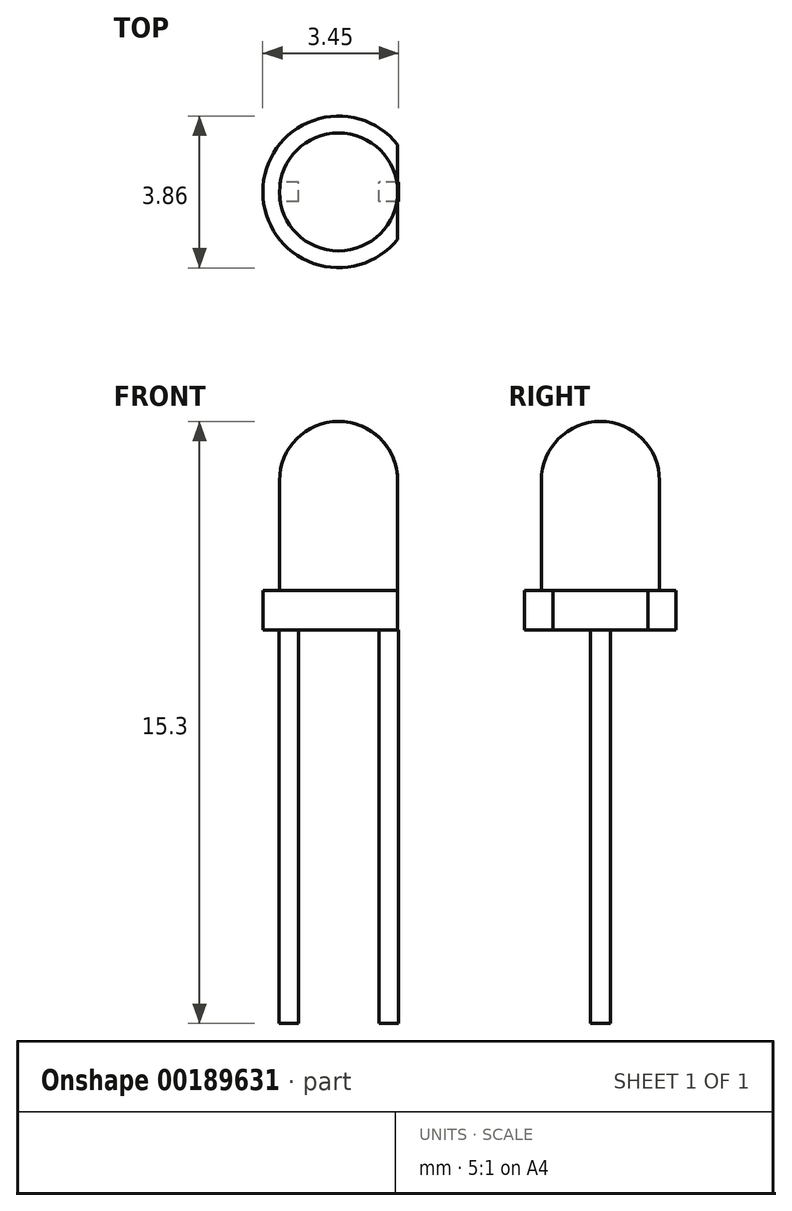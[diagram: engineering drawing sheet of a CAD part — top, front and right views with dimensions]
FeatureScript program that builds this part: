
annotation { "Feature Type Name" : "Feature", "Feature Type Description" : "" }
export const myFeature = defineFeature(function(context is Context, id is Id, definition is map)
    precondition{}
    {
        {
            var Q0;
            Q0=qCreatedBy(makeId("Front.planeOp"),FACE);
            var sketch = newSketch(context, id + "F0", { "sketchPlane" : qUnion([Q0])});
            skLineSegment(sketch, "E0", {"start": v(0, 0) * mm, "end": v(0, 5.3) * mm});
            skLineSegment(sketch, "E1", {"start": v(0, 0) * mm, "end": v(1.93, 0) * mm});
            skLineSegment(sketch, "E2", {"start": v(1.93, 0) * mm, "end": v(1.93, 1) * mm});
            skLineSegment(sketch, "E3", {"start": v(1.93, 1) * mm, "end": v(1.5, 1) * mm});
            skLineSegment(sketch, "E4", {"start": v(1.5, 1) * mm, "end": v(1.5, 3.8) * mm});
            skArc(sketch, "E5", {"start": v(1.5, 3.8) * mm, "mid": v(1.06, 4.86) * mm, "end": v(0, 5.3) * mm});
            skLineSegment(sketch, "E6", {"start": v(1.5, 3.8) * mm, "end": v(0.5, 3.8) * mm, "construction": true});
            skSolve(sketch);
        }
        {
            var Q0;
            Q0=qSketchRegion(id+"F0",true);
            var Q1;
            Q1=sQuery(id+"F0.wireOp",EDGE,"E0");
            revolve(context, id + "F1", {"entities" : qUnion([Q0]), "axis" : qUnion([Q1]), "revolveType" : RevolveType.FULL});
        }
        {
            var Q0;
            Q0=makeQuery(id+"F1.opRevolve","SWEPT_FACE",FACE,{"disambiguationData":[OSD([sQuery(id+"F0.wireOp",EDGE,"E3")])]});
            var sketch = newSketch(context, id + "F2", { "sketchPlane" : qUnion([Q0])});
            skLineSegment(sketch, "E7.bottom", {"start": v(1.5, 2.54) * mm, "end": v(3.1, 2.54) * mm});
            skLineSegment(sketch, "E7.top", {"start": v(1.5, -2.28) * mm, "end": v(3.1, -2.28) * mm});
            skLineSegment(sketch, "E7.left", {"start": v(1.5, 2.54) * mm, "end": v(1.5, -2.28) * mm});
            skLineSegment(sketch, "E7.right", {"start": v(3.1, 2.54) * mm, "end": v(3.1, -2.28) * mm});
            skSolve(sketch);
        }
        {
            var Q0;
            Q0=qSketchRegion(id+"F2",true);
            extrude(context, id + "F3", {"entities" : qUnion([Q0]), "operationType" : NewBodyOperationType.REMOVE, "oppositeDirection" : true, "depth" : 25 * mm});
        }
        {
            var Q0;
            Q0=qCreatedBy(makeId("Top.planeOp"),FACE);
            var sketch = newSketch(context, id + "F4", { "sketchPlane" : qUnion([Q0])});
            skLineSegment(sketch, "E8.bottom", {"start": v(-1.02, -0.25) * mm, "end": v(-1.52, -0.25) * mm});
            skLineSegment(sketch, "E8.top", {"start": v(-1.02, 0.25) * mm, "end": v(-1.52, 0.25) * mm});
            skLineSegment(sketch, "E8.left", {"start": v(-1.02, -0.25) * mm, "end": v(-1.02, 0.25) * mm});
            skLineSegment(sketch, "E8.right", {"start": v(-1.52, -0.25) * mm, "end": v(-1.52, 0.25) * mm});
            skPoint(sketch, "E8.middle", {"position": v(-1.27, 0) * mm});
            skLineSegment(sketch, "E9.bottom", {"start": v(1.52, -0.25) * mm, "end": v(1.02, -0.25) * mm});
            skLineSegment(sketch, "E9.top", {"start": v(1.52, 0.25) * mm, "end": v(1.02, 0.25) * mm});
            skLineSegment(sketch, "E9.left", {"start": v(1.52, -0.25) * mm, "end": v(1.52, 0.25) * mm});
            skLineSegment(sketch, "E9.right", {"start": v(1.02, -0.25) * mm, "end": v(1.02, 0.25) * mm});
            skPoint(sketch, "E9.middle", {"position": v(1.27, 0) * mm});
            skSolve(sketch);
        }
        {
            var Q0;
            Q0=qSketchRegion(id+"F4",true);
            extrude(context, id + "F5", {"entities" : qUnion([Q0]), "operationType" : NewBodyOperationType.ADD, "oppositeDirection" : true, "depth" : 10 * mm});
        }
    });
